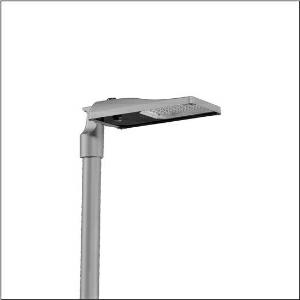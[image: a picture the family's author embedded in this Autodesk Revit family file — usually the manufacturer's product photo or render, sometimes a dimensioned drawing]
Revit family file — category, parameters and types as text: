
# Revit family: streetlight_sl_31_mini___st1_0a_5xh2d31t08ga_2aba
name_source: partatom
category: Lighting Fixtures
units: mm (PartAtom-declared; Revit-internal decimal feet)

## family parameters
Cut with Voids When Loaded = No
Host = Face
Light Source = No
Part Type = Normal
Room Calculation Point = No
Round Connector Dimension = Use Diameter
Shared = No

## types (1)
- --- (1 x LED, 5880 lm, 39.3 W, 3000K)
    Apparent Load = 39 VA
    CIE Flux Codes = 37 72 97 100 100
    Color Rendering = 70
    Color Temperature = 3000K
    Default Elevation = 1800 mm
    Description = Streetlight SL 31 mini D4i, Desk-Remote mast luminaire for post-top, side-entry; light control with lens of PMMA; light distribution: ST1.0a, direct asymmetric distribution, for standard-compliant lighting for roads and squares; LED: luminous flux: 5.880lm, light colour: 730, colour temperature: 3000K; luminous efficacy: 149,6lm/W; control: pre-setting: logarithmic dimming characteristic, flexible luminous flux parameterisation, time-dependent luminous flux control, constant luminous flux control, power reduction, intelligent temperature release in ECG and LED module, overheat protection; luminaire housing, of diecast aluminium, SITECO metallic grey (DB 702S), corrosivity category C5 high according to DIN EN ISO 12944; cover of toughened safety glass, transparent, mast flange of diecast aluminium, SITECO metallic grey (DB 702S), spigot size: 76/60mm, mast flange included unmounted; with cable H07RN-F 2x 1.5mm², cable length: 6,5m, connection cable pre-assembled; mains connection: 220..240V, AC, 50/60Hz; power consumption (at start of service life): 39,3W / (at end of service life): 40,7W / (with reduced operation 50%): 18,1W; protection rating (complete): IP66; insulation class (complete): insulation class II (safety insulation); impact resistance: IK09; certification: CE, ENEC, ENEC+, VDE, UKCA, ZD4i; permissible operating ambient temperature for outdoor applications: -40..+50°C; packaging unit: 1 piece

Light Distribution: ST1.0a
    Height = 76 mm
    Lamp = 1 x LED
    Lamp Light Flux = 5880 lm
    Lamp Power = 39.3 W
    Lamp count = 1
    Length = 547 mm
    Luminous efficacy = 150 lm/W
    Manufacturer = Siteco
    ModVariant = No
    Model = 5XH2D31T08GA
    Number of Poles = 1
    OnlyDefault = Yes
    Power Factor = 1
    Product Name = Streetlight SL 31 mini | ST1.0a
    Product group = mast luminaire | pylon top
    ProductGroupID = 6100
    Protection Class = Protection class II
    Protection Degree = IP 66
    RLX_Detail_Level = 1
    RLX_Emergency_Light_Flux = 0 lm
    RLX_Emergency_Type = 0
    RLX_Emergency_Type_DB = No
    RlxData = <blob elided: 39869 chars, md5=daedf586>
    Socket = socket
    Standby Power = 0 W
    System Light Flux = 5880 lm
    System Power = 39 W
    Type Comments = factory setting: luminous flux: 100 % | dim-lin: 254 | 798 mA
    Type Image = l_1300332.jpg
    URL = http://relux.com
    VarID = @adj_061413
    Voltage = 0 V
    Weight = 0.00 kg
    Width = 265 mm

## geometry (parser evidence)
native form markers: Blend x4, Sweep x9
no freeform markers — native parametric forms only
